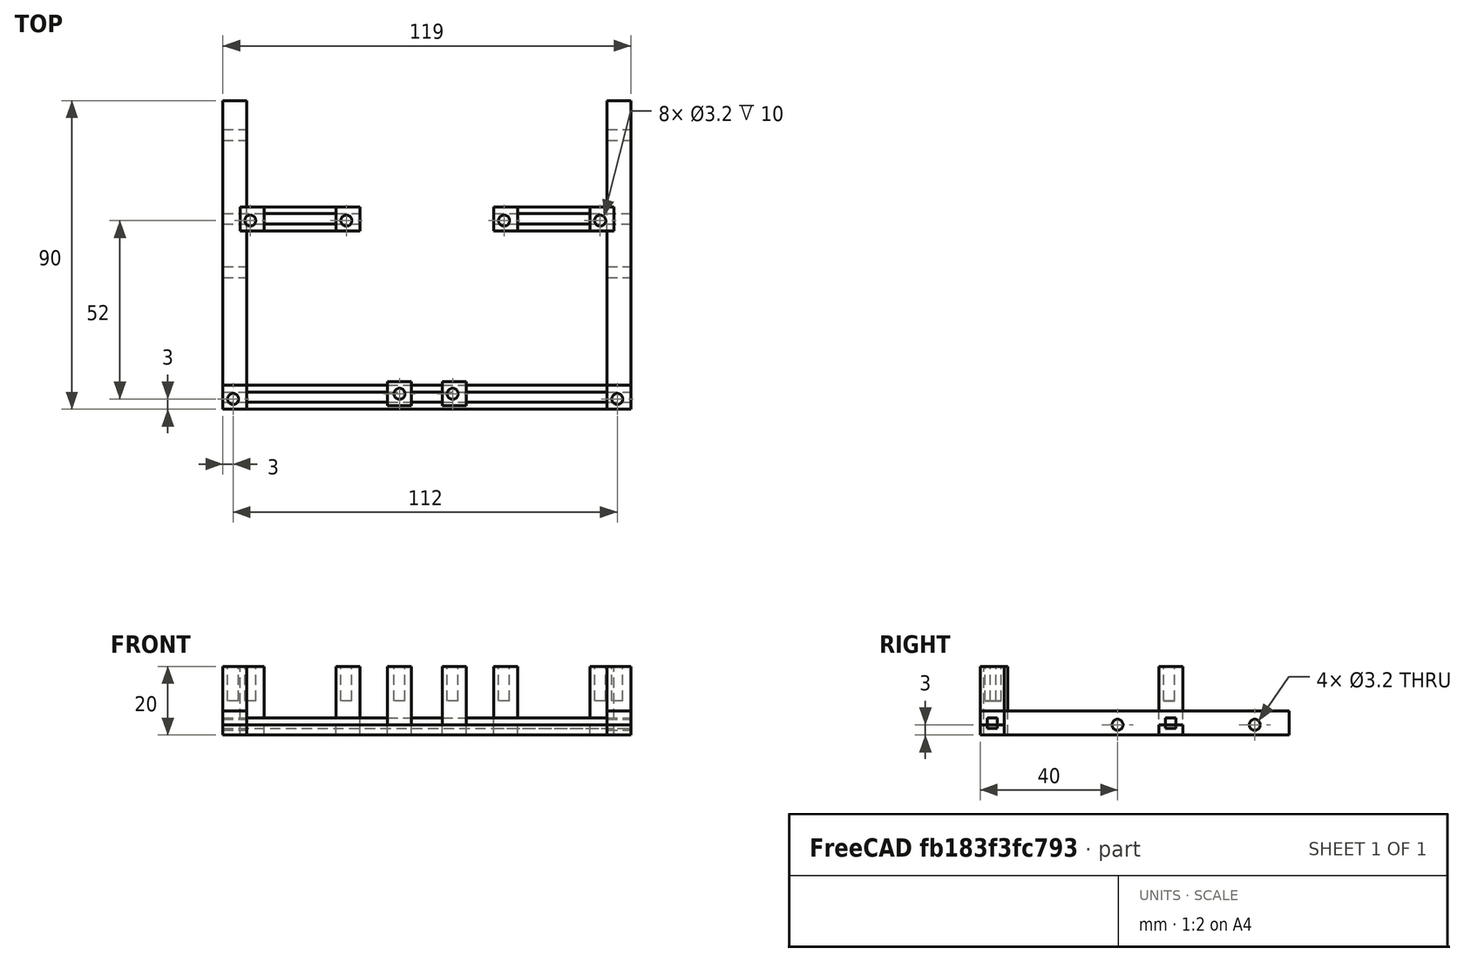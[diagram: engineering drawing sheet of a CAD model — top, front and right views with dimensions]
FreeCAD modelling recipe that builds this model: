
FCSTD DOCUMENT  (FreeCAD 0.15R4671 (Git))
Label: support_double_carte
License: All rights reserved
LicenseURL: http://fr.wikipedia.org/wiki/<copyright redacted>
objects: Part::Box×16, Part::Cylinder×12, Part::Cut×12
note: 40 computed .brp shape members not serialized (recipe doc carries the construction recipe); baked Part::Feature solids carry a one-line shape summary decoded from their .brp

FEATURE [Part::Box] Box  label="Cube"
  Height = 3
  Length = 119
  Width = 7
FEATURE [Part::Box] Box001  label="Cube001"
  Height = 3
  Length = 119
  Placement = pos=(0,2,2) rot=(0,0,1;0rad)
  Width = 3
FEATURE [Part::Box] Box002  label="Cube002"
  Height = 20
  Length = 7
  Width = 7
FEATURE [Part::Box] Box003  label="Cube003"
  Height = 20
  Length = 7
  Placement = pos=(112,0,0) rot=(0,0,1;0rad)
  Width = 7
FEATURE [Part::Box] Box004  label="Cube004"
  Height = 20
  Length = 7
  Placement = pos=(48,1,0) rot=(0,0,1;0rad)
  Width = 7
FEATURE [Part::Box] Box005  label="Cube005"
  Height = 20
  Length = 7
  Placement = pos=(64,1,0) rot=(0,0,1;0rad)
  Width = 7
FEATURE [Part::Box] Box006  label="Cube006"
  Height = 7
  Length = 90
  Placement = pos=(7,0,0) rot=(0,0,1;1.5708rad)
  Width = 7
FEATURE [Part::Box] Box007  label="Cube007"
  Height = 7
  Length = 90
  Placement = pos=(119,0,0) rot=(0,0,1;1.5708rad)
  Width = 7
FEATURE [Part::Box] Box010  label="Cube010"
  Height = 3
  Length = 40
  Placement = pos=(0,54,2) rot=(0,0,1;0rad)
  Width = 3
FEATURE [Part::Box] Box011  label="Cube011"
  Height = 3
  Length = 40
  Placement = pos=(0,52,0) rot=(0,0,1;0rad)
  Width = 7
FEATURE [Part::Box] Box012  label="Cube012"
  Height = 3
  Length = 40
  Placement = pos=(79,54,2) rot=(0,0,1;0rad)
  Width = 3
FEATURE [Part::Box] Box013  label="Cube013"
  Height = 3
  Length = 40
  Placement = pos=(79,52,0) rot=(0,0,1;0rad)
  Width = 7
FEATURE [Part::Box] Box014  label="Cube014"
  Height = 20
  Length = 7
  Placement = pos=(107,52,0) rot=(0,0,1;0rad)
  Width = 7
FEATURE [Part::Box] Box015  label="Cube015"
  Height = 20
  Length = 7
  Placement = pos=(33,52,0) rot=(0,0,1;0rad)
  Width = 7
FEATURE [Part::Box] Box016  label="Cube016"
  Height = 20
  Length = 7
  Placement = pos=(5,52,0) rot=(0,0,1;0rad)
  Width = 7
FEATURE [Part::Box] Box017  label="Cube017"
  Height = 20
  Length = 7
  Placement = pos=(79,52,0) rot=(0,0,1;0rad)
  Width = 7
FEATURE [Part::Cylinder] Cylinder  label="Cylindre"
  Angle = 360
  Height = 20
  Placement = pos=(3,3,10) rot=(0,0,1;0rad)
  Radius = 1.6
FEATURE [Part::Cylinder] Cylinder001  label="Cylindre001"
  Angle = 360
  Height = 20
  Placement = pos=(8,55,10) rot=(0,0,1;0rad)
  Radius = 1.6
FEATURE [Part::Cylinder] Cylinder002  label="Cylindre002"
  Angle = 360
  Height = 20
  Placement = pos=(36,55,10) rot=(0,0,1;0rad)
  Radius = 1.6
FEATURE [Part::Cylinder] Cylinder003  label="Cylindre003"
  Angle = 360
  Height = 20
  Placement = pos=(82,55,10) rot=(0,0,1;0rad)
  Radius = 1.6
FEATURE [Part::Cylinder] Cylinder004  label="Cylindre004"
  Angle = 360
  Height = 20
  Placement = pos=(110,55,10) rot=(0,0,1;0rad)
  Radius = 1.6
FEATURE [Part::Cylinder] Cylinder005  label="Cylindre005"
  Angle = 360
  Height = 20
  Placement = pos=(115,3,10) rot=(0,0,1;0rad)
  Radius = 1.6
FEATURE [Part::Cylinder] Cylinder006  label="Cylindre006"
  Angle = 360
  Height = 20
  Placement = pos=(67,4.5,10) rot=(0,0,1;0rad)
  Radius = 1.6
FEATURE [Part::Cylinder] Cylinder007  label="Cylindre007"
  Angle = 360
  Height = 20
  Placement = pos=(51.5,4.5,10) rot=(0,0,1;0rad)
  Radius = 1.6
FEATURE [Part::Cut] Cut
  Base = -> Box002
  Tool = -> Cylinder
FEATURE [Part::Cut] Cut001
  Base = -> Box014
  Tool = -> Cylinder004
FEATURE [Part::Cut] Cut002
  Base = -> Box015
  Tool = -> Cylinder002
FEATURE [Part::Cut] Cut003
  Base = -> Box016
  Tool = -> Cylinder001
FEATURE [Part::Cut] Cut004
  Base = -> Box017
  Tool = -> Cylinder003
FEATURE [Part::Cut] Cut005
  Base = -> Box005
  Tool = -> Cylinder006
FEATURE [Part::Cut] Cut006
  Base = -> Box004
  Tool = -> Cylinder007
FEATURE [Part::Cut] Cut007
  Base = -> Box003
  Tool = -> Cylinder005
FEATURE [Part::Cylinder] Cylinder008  label="Cylindre008"
  Angle = 360
  Height = 20
  Placement = pos=(-4,40,3) rot=(0,1,0;1.5708rad)
  Radius = 1.6
FEATURE [Part::Cylinder] Cylinder009  label="Cylindre009"
  Angle = 360
  Height = 20
  Placement = pos=(-4,80,3) rot=(0,1,0;1.5708rad)
  Radius = 1.6
FEATURE [Part::Cylinder] Cylinder010  label="Cylindre010"
  Angle = 360
  Height = 20
  Placement = pos=(105,40,3) rot=(0,1,0;1.5708rad)
  Radius = 1.6
FEATURE [Part::Cylinder] Cylinder011  label="Cylindre011"
  Angle = 360
  Height = 20
  Placement = pos=(105,80,3) rot=(0,1,0;1.5708rad)
  Radius = 1.6
FEATURE [Part::Cut] Cut008
  Base = -> Box006
  Tool = -> Cylinder008
FEATURE [Part::Cut] Cut009
  Base = -> Cut008
  Tool = -> Cylinder009
FEATURE [Part::Cut] Cut010
  Base = -> Box007
  Tool = -> Cylinder010
FEATURE [Part::Cut] Cut011
  Base = -> Cut010
  Tool = -> Cylinder011
